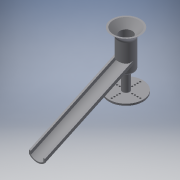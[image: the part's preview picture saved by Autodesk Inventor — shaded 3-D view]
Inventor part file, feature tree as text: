
AUTODESK INVENTOR PART (.ipt)
format: ipt  version: 2019 (Build 230136000, 136)  size: 325,632 bytes
history: native  units: mm
features: sketch x10, extrude x7, sweep x4, other x2, fillet x2, mirror x1, pattern_circular x1
ambient origin geometry x8: Origin, YZ Plane, XZ Plane, XY Plane, X Axis, Y Axis, Z Axis, Center Point
bodies: Solide1 (feature_tree)
feature tree (27):
  sketch  "Esquisse2"
  sketch  "Esquisse1"
  sweep  "Balayage1"
  sweep  "Balayage2"
  extrude  "Extrusion1"  Depth=20.071286mm
  other  "Plan de construction1"
  sketch  "Esquisse4"
  extrude  "Extrusion2"  Depth=7.0mm
  sweep  "Balayage3"
  extrude  "Extrusion3"  Depth=2.0mm
  extrude  "Extrusion4"  Depth=4.0mm
  sweep  "Balayage4"
  extrude  "Extrusion5"  TaperAngle=0.0deg  [1 undecoded]
  extrude  "Extrusion6"  Depth=15.0mm TaperAngle=0.0deg
  fillet  "Congé1"  Radius=10.0mm
  extrude  "Extrusion7"  Depth=11.34464mm
  mirror  "Symétrie1"
  pattern_circular  "Réseau circulaire1"  [2 undecoded]
  other  "Révolution1"
  fillet  "Congé2"  Radius=20.0mm
  sketch  "Esquisse3"
  sketch  "Esquisse6"
  sketch  "Esquisse7"
  sketch  "Esquisse9"
  sketch  "Esquisse10"
  sketch  "Esquisse11"
  sketch  "Esquisse12"
note: 3 required parameter values undecoded (feature->parameter linkage not recoverable at this tier; creation-order binding heuristic only, values carry confidence <= 0.55)
